# Revit family: 3-400-xxxx - Dario Wall Sconce
name_source: partatom
category: Luminarias
units: mm (PartAtom-declared; Revit-internal decimal feet)

## family parameters
Anfitrión = Muro
Compartido = No
Corte con vacíos al cargar = No
Cota de conector redondo = Diámetro de uso
Número OmniClass = 23.80.70.00
Origen de luz = Sí
Punto de cálculo de habitación = No
Siempre vertical = Sí
Tipo de pieza = Normal
Título OmniClass = Lighting

## types (4) — shared parameters
Archivo de red fotométrica = Dario 3-400-xx.ies
Cambio de temperatura de color de luz atenuada = <Ninguno>
Comentarios de vataje = 1 x 6.83 W at 120 V
Diffusers = Matte White Acrylic
Fabricante = Oxygen Lighting and Fans
Filtro de color = 16777215
Lámpara = LED Array
Modelo = 3-400-xxxx / Dario Wall Sconce
References = Ref. 3 = 120 V / Ref. 37 = 277 V
URL = www.oxygenlighting.com
Voltage = 120 V
Voltage Input = 120 V or 277 V - 50/60 Hz
Ángulo de inclinación = 90.00°
zero-valued in all types: Elevación por defecto

## per-type parameters (varying)
| type | Metal Finish | Metal finish 2 |
| 3-400-640 / White - Aged Brassl - Matte White Acrylic | 40 - Aged Brass | 6 - White |
| 3-400-1524 / Black - Satin Nickel - Matte White Acrylic | 24 - Satin Nickel | 15 - Black |
| 3-400-1540 / Black - Aged Brassl - Matte White Acrylic | 40 - Aged Brass | 15 - Black |
| 3-400-1541 / Black - Weathered Oak - Matte White Acrylic | 40 - Aged Brass | 15 - Black |

## geometry (parser evidence)
native form markers: Sweep x4
no freeform markers — native parametric forms only
